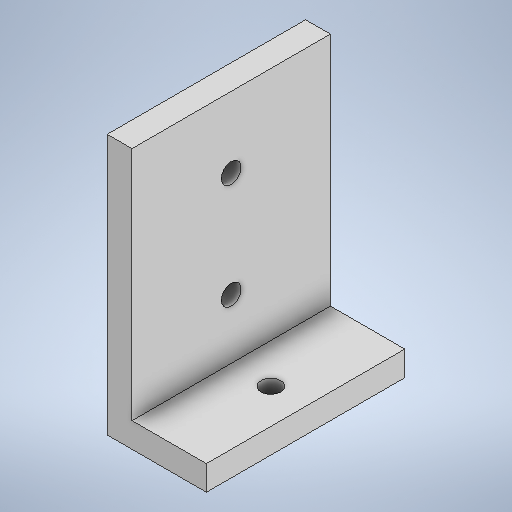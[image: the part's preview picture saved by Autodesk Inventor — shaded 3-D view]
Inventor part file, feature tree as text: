
AUTODESK INVENTOR PART (.ipt)
format: ipt  version: 2025.2 (Build 292293000, 293)  size: 226,816 bytes
history: native  units: mm
features: extrude x3, sketch x3, pattern_linear x1
ambient origin geometry x8: Origin, YZ Plane, XZ Plane, XY Plane, X Axis, Y Axis, Z Axis, Center Point
bodies: Solid1 (feature_tree)
feature tree (7):
  extrude  "Extrusion1"  Depth=10.0mm
  extrude  "Extrusion2"  Depth=30.0mm
  pattern_linear  "Rectangular Pattern1"  Count1=4  [1 undecoded]
  extrude  "Extrusion3"  Depth=80.0mm TaperAngle=0.0deg
  sketch  "Sketch1"  dims[d0=105.0mm d1=10.0mm]
  sketch  "Sketch2"  dims[d2=95.0mm d3=30.0mm]
  sketch  "Sketch3"  dims[d4=10.0mm d5=40.0mm d6=80.0mm d7=0.0mm d8=8.0mm d9=34.0mm d10=40.0mm d11=10.0mm d12=0.0mm d13=20.0mm d15=42.5mm d16=8.0mm d17=26.0mm d18=40.0mm d19=10.0mm d20=0.0mm]
note: 1 required parameter value undecoded (feature->parameter linkage not recoverable at this tier; creation-order binding heuristic only, values carry confidence <= 0.55)
